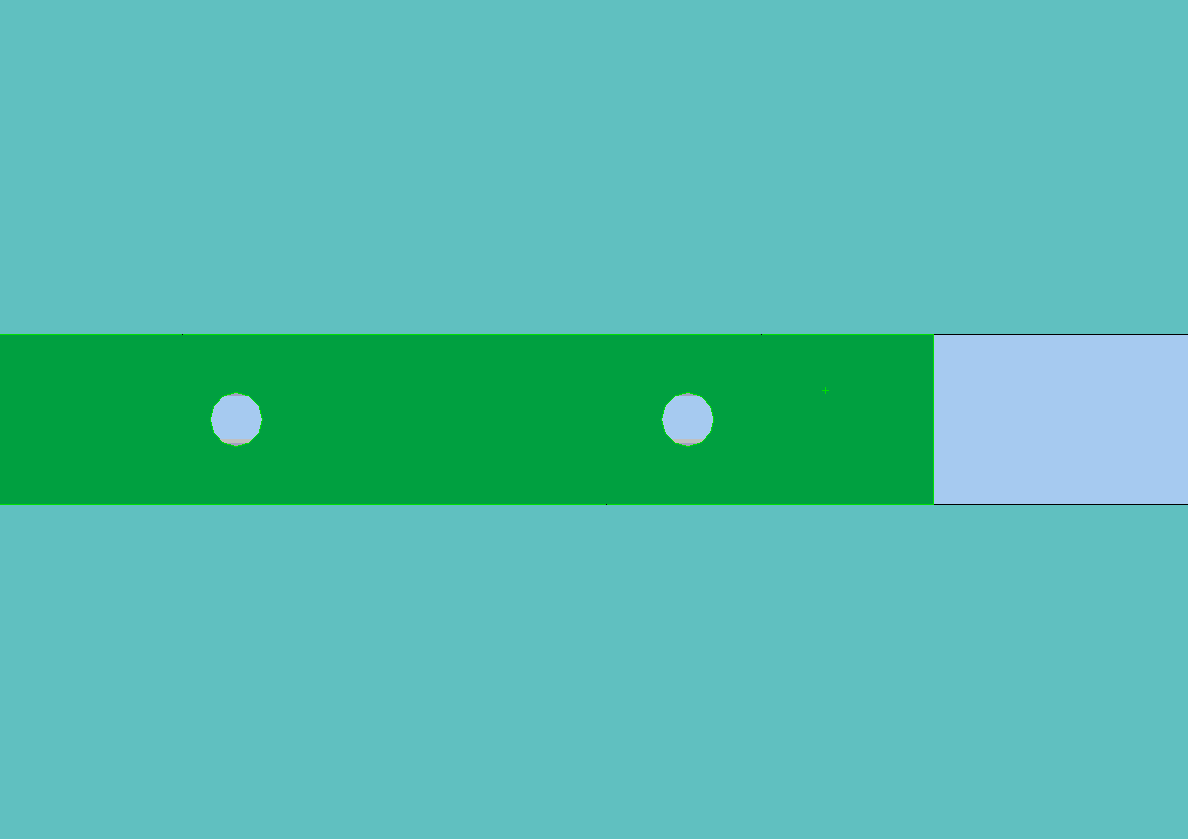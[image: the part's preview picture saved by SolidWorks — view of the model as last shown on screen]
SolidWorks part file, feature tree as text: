
SOLIDWORKS PART (.sldprt)
format: sldprt  version: not decoded by parser v0  size: 279,552 bytes
history: native  units: mm
features: sketch x6, cut_extrude x5, material x1, extrude x1 (+13 scaffold rows collapsed)
feature tree (26):
  scaffold x13  (default folders/planes/origin — collapsed)
  material  "7079 Alloy"
  sketch  "Sketch1"  dims[D1=76.2mm D2=73.025mm]
  extrude  "Extrude1"  Depth=12.7mm
  sketch  "Sketch8"  dims[c1.D1=6.35mm c1.D2=6.35mm c1.D3=6.35mm c1.D4=6.35mm c1.D5=6.35mm c1.D6=4.7625mm c1.D7=4.7625mm c1.D8=14.224mm c2.D4=6.35mm c2.D22=~2.52974mm c2.D28=1.778mm c3.D4=7.1374mm c3.D9=7.1374mm c3.D10=7.1374mm c3.D11=69.0626mm c3.D12=7.1374mm c3.D13=7.1374mm c3.D14=34.925mm c3.D15=65.8876mm c3.D16=~38.094982mm c3.D17=34.925mm c3.D18=69.0626mm c3.D19=69.0626mm c3.D20=34.925mm c3.D21=65.8876mm c3.D22=25.019mm c3.D23=25.019mm c3.D24=25.019mm c3.D25=~23.141045mm c4.D24=25.019mm c4.D25=25.019mm c4.D26=25.019mm c4.D27=25.019mm c4.D28=25.019mm c4.D29=~30.967618mm c4.D23=45.0deg c5.D25=45.0deg c5.D27=45.0deg c5.D29=45.0deg]
  cut_extrude  "Cut-Extrude5"  Depth=12.7mm
  sketch  "Sketch11"  dims[D1=10.414mm D2=10.414mm D3=10.414mm D4=10.414mm D5=7.1374mm D6=7.1374mm]
  cut_extrude  "Cut-Extrude6"  Depth=6.35mm
  sketch  "Sketch13"  dims[D1=34.925mm]
  cut_extrude  "Cut-Extrude7"  Depth=4.2545mm
  sketch  "Sketch14"  dims[D1=25.4mm]
  cut_extrude  "Cut-Extrude8"  Depth=0.254mm
  sketch  "Sketch15"  dims[c1.D1=~26.624255mm c1.D2=~32.480356mm c1.D3=~30.494806mm c2.D2=36.5125mm c2.D3=36.5125mm c2.D4=6.35mm]
  cut_extrude  "Cut-Extrude9"  [1 undecoded]
decode coverage: 11 of 12 modeling features carry decoded parameters
note: ~ marks probable driven/reference dimensions
note: 1 parameter value undecoded
note: suppression state not decoded; provenance and decode notes live in map.json
